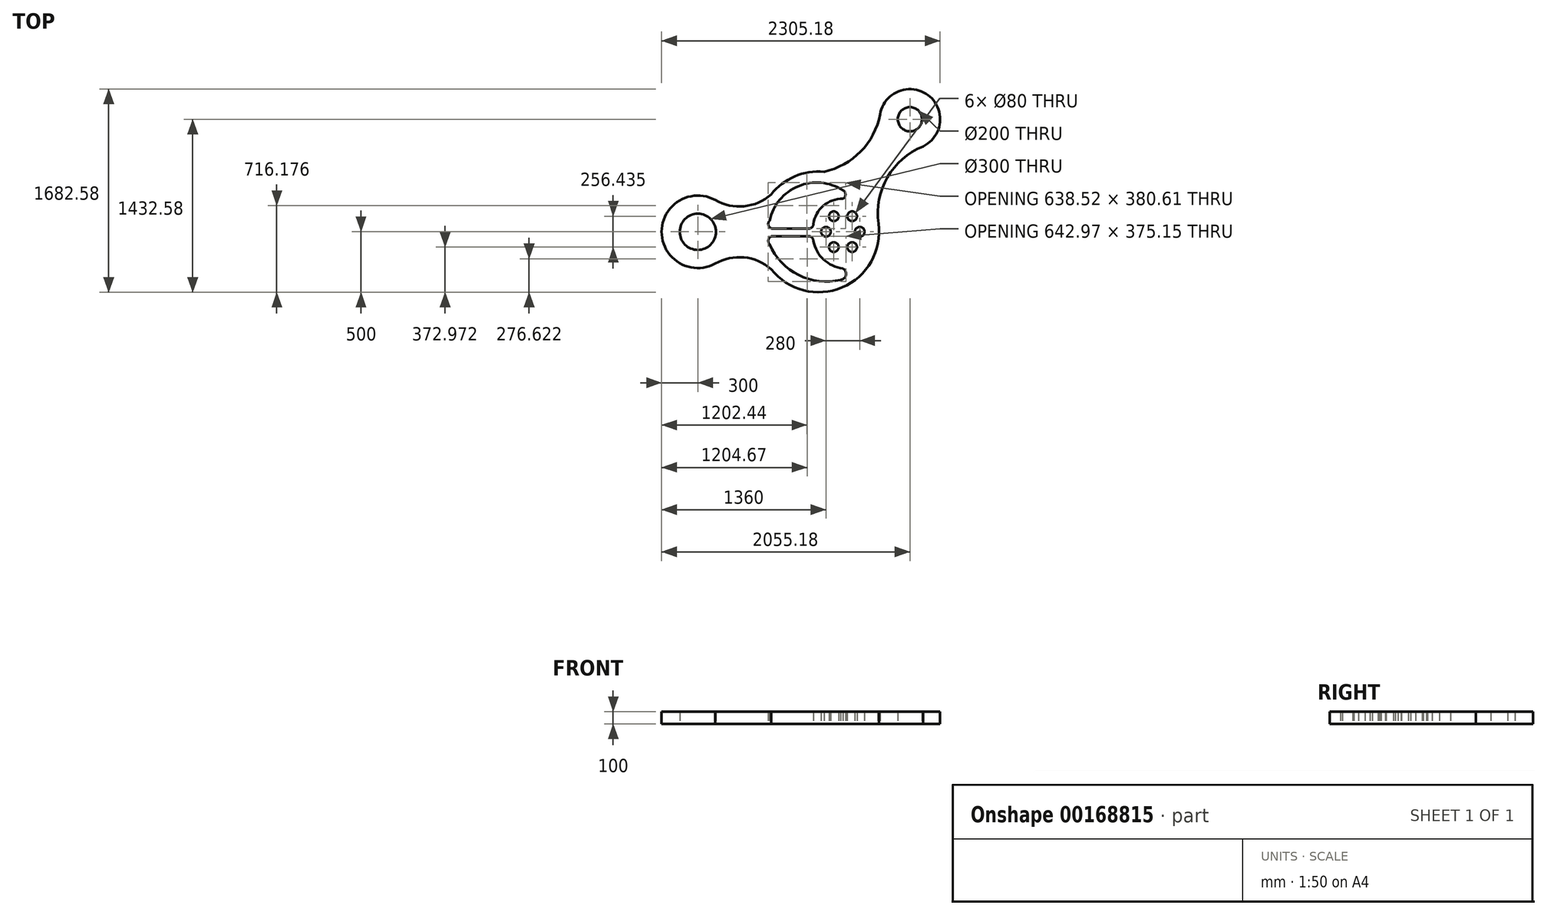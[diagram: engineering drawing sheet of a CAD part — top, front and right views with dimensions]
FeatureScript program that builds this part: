
annotation { "Feature Type Name" : "Feature", "Feature Type Description" : "" }
export const myFeature = defineFeature(function(context is Context, id is Id, definition is map)
    precondition{}
    {
        {
            var Q0;
            Q0=qCreatedBy(makeId("Top.planeOp"),FACE);
            var sketch = newSketch(context, id + "F0", { "sketchPlane" : qUnion([Q0])});
            skLineSegment(sketch, "E0", {"start": v(200, 0) * mm, "end": v(-1981.3, 0) * mm});
            skLineSegment(sketch, "E1", {"start": v(0, 0) * mm, "end": v(874.41, 1079.81) * mm});
            skCircle(sketch, "E2", {"center": v(755.18, 932.58) * mm, "radius": 100 * mm});
            skCircle(sketch, "E3", {"center": v(755.18, 932.58) * mm, "radius": 250 * mm});
            skCircle(sketch, "E4", {"center": v(0, 0) * mm, "radius": 500 * mm});
            skCircle(sketch, "E5", {"center": v(-1000, 0) * mm, "radius": 150 * mm});
            skCircle(sketch, "E6", {"center": v(-1000, 0) * mm, "radius": 300 * mm});
            skArc(sketch, "E7", {"start": v(-856.64, 263.53) * mm, "mid": v(-617.37, 211.9) * mm, "end": v(-392.82, 309.34) * mm});
            skArc(sketch, "E8", {"start": v(-392.82, -309.34) * mm, "mid": v(-617.37, -211.9) * mm, "end": v(-856.64, -263.53) * mm});
            skArc(sketch, "E9", {"start": v(43.8, 498.08) * mm, "mid": v(347.86, 665.32) * mm, "end": v(508.46, 972.94) * mm});
            skArc(sketch, "E10", {"start": v(864.48, 707.73) * mm, "mid": v(569.68, 451.16) * mm, "end": v(495.43, 67.47) * mm});
            skCircle(sketch, "E11", {"center": v(200, 0) * mm, "radius": 220 * mm});
            skCircle(sketch, "E12", {"center": v(340, 0) * mm, "radius": 40 * mm});
            skCircle(sketch, "E13", {"center": v(60, 0) * mm, "radius": 40 * mm});
            skCircle(sketch, "E14", {"center": v(125.2, -127.03) * mm, "radius": 40 * mm});
            skCircle(sketch, "E15", {"center": v(277.06, -127.03) * mm, "radius": 40 * mm});
            skCircle(sketch, "E16", {"center": v(277.06, 129.4) * mm, "radius": 40 * mm});
            skCircle(sketch, "E17", {"center": v(125.2, 129.4) * mm, "radius": 40 * mm});
            skArc(sketch, "E18", {"start": v(200, 344.87) * mm, "mid": v(-169.16, 377.43) * mm, "end": v(-406.61, 92.9) * mm});
            skLineSegment(sketch, "E19", {"start": v(-83.93, 25.87) * mm, "end": v(-377.13, 25.87) * mm});
            skArc(sketch, "E20", {"start": v(-406.61, 92.9) * mm, "mid": v(-413.75, 49.77) * mm, "end": v(-377.13, 25.87) * mm});
            skArc(sketch, "E21", {"start": v(200, 273.73) * mm, "mid": v(37.99, 215.88) * mm, "end": v(-43.95, 64.62) * mm});
            skArc(sketch, "E22", {"start": v(-83.93, 25.87) * mm, "mid": v(-56.1, 37.15) * mm, "end": v(-43.95, 64.62) * mm});
            skArc(sketch, "E23", {"start": v(200, 273.73) * mm, "mid": v(221.7, 309.3) * mm, "end": v(200, 344.87) * mm});
            skLineSegment(sketch, "E24", {"start": v(-377.13, -35.8) * mm, "end": v(-83.93, -35.8) * mm});
            skArc(sketch, "E25", {"start": v(-377.13, -35.8) * mm, "mid": v(-413.75, -59.7) * mm, "end": v(-406.61, -102.83) * mm});
            skArc(sketch, "E26", {"start": v(-43.95, -77.05) * mm, "mid": v(41.57, -229.75) * mm, "end": v(200, -304.12) * mm});
            skArc(sketch, "E27", {"start": v(-43.95, -77.05) * mm, "mid": v(-55.2, -47.96) * mm, "end": v(-83.93, -35.8) * mm});
            skArc(sketch, "E28", {"start": v(-406.61, -102.83) * mm, "mid": v(-165.7, -357.89) * mm, "end": v(182.87, -397.69) * mm});
            skArc(sketch, "E29", {"start": v(182.87, -397.69) * mm, "mid": v(225.8, -357.2) * mm, "end": v(200, -304.12) * mm});
            skSolve(sketch);
        }
        {
            var Q0;
            {var subQ1=sQuery(id+"F0.wireOp",EDGE,"E6");var subQ3=sQuery(id+"F0.wireOp",EDGE,"E0");var subQ4=makeQuery(id+"F0.imprint","INTERSECT",VERTEX,{"disambiguationData":[OD(1.0)],"derivedFrom":[subQ3,subQ1]});Q0=makeQuery(id+"F0.imprint","IMPRINT",FACE,{"disambiguationData":[TD([[makeQuery(id+"F0.imprint","IMPRINT",EDGE,{"disambiguationData":[TD([[subQ4,-1.0]])],"derivedFrom":subQ3}),-1.0]])]});}
            var Q1;
            {var subQ1=sQuery(id+"F0.wireOp",EDGE,"E6");var subQ3=sQuery(id+"F0.wireOp",EDGE,"E0");var subQ9=makeQuery(id+"F0.imprint","INTERSECT",VERTEX,{"disambiguationData":[OD(1.0)],"derivedFrom":[subQ3,subQ1]});Q1=makeQuery(id+"F0.imprint","IMPRINT",FACE,{"disambiguationData":[TD([[makeQuery(id+"F0.imprint","IMPRINT",EDGE,{"disambiguationData":[TD([[subQ9,-1.0]])],"derivedFrom":subQ3}),1.0]])]});}
            var Q2;
            {var subQ0=sQuery(id+"F0.wireOp",EDGE,"E4");var subQ1=sQuery(id+"F0.wireOp",EDGE,"E0");var subQ2=makeQuery(id+"F0.imprint","INTERSECT",VERTEX,{"derivedFrom":[subQ1,subQ0]});Q2=makeQuery(id+"F0.imprint","IMPRINT",FACE,{"disambiguationData":[TD([[makeQuery(id+"F0.imprint","IMPRINT",EDGE,{"disambiguationData":[TD([[subQ2,-1.0]])],"derivedFrom":subQ1}),1.0]])]});}
            var Q3;
            {var subQ0=sQuery(id+"F0.wireOp",EDGE,"E4");var subQ1=sQuery(id+"F0.wireOp",EDGE,"E0");var subQ2=makeQuery(id+"F0.imprint","INTERSECT",VERTEX,{"derivedFrom":[subQ1,subQ0]});Q3=makeQuery(id+"F0.imprint","IMPRINT",FACE,{"disambiguationData":[TD([[makeQuery(id+"F0.imprint","IMPRINT",EDGE,{"disambiguationData":[TD([[subQ2,-1.0]])],"derivedFrom":subQ1}),-1.0]])]});}
            var Q4;
            Q4=makeQuery(id+"F0.imprint","IMPRINT",FACE,{"disambiguationData":[TD([[makeQuery(id+"F0.imprint","IMPRINT",EDGE,{"derivedFrom":sQuery(id+"F0.wireOp",EDGE,"E18")}),-1.0]])]});
            var Q5;
            Q5=makeQuery(id+"F0.imprint","IMPRINT",FACE,{"disambiguationData":[TD([[makeQuery(id+"F0.imprint","IMPRINT",EDGE,{"derivedFrom":sQuery(id+"F0.wireOp",EDGE,"E24")}),1.0]])]});
            var Q6;
            Q6=makeQuery(id+"F0.imprint","IMPRINT",FACE,{"disambiguationData":[TD([[makeQuery(id+"F0.imprint","IMPRINT",EDGE,{"derivedFrom":sQuery(id+"F0.wireOp",EDGE,"E12")}),-1.0]])]});
            var Q7;
            {var subQ1=sQuery(id+"F0.wireOp",EDGE,"E0");var subQ3=sQuery(id+"F0.wireOp",EDGE,"E1");var subQ7=makeQuery(id+"F0.imprint","INTERSECT",VERTEX,{"derivedFrom":[subQ1,subQ3]});Q7=makeQuery(id+"F0.imprint","IMPRINT",FACE,{"disambiguationData":[TD([[makeQuery(id+"F0.imprint","IMPRINT",EDGE,{"disambiguationData":[TD([[subQ7,-1.0]])],"derivedFrom":subQ1}),-1.0]])]});}
            var Q8;
            {var subQ0=sQuery(id+"F0.wireOp",EDGE,"E3");var subQ1=sQuery(id+"F0.wireOp",EDGE,"E1");var subQ2=makeQuery(id+"F0.imprint","INTERSECT",VERTEX,{"derivedFrom":[subQ1,subQ0]});Q8=makeQuery(id+"F0.imprint","IMPRINT",FACE,{"disambiguationData":[TD([[makeQuery(id+"F0.imprint","IMPRINT",EDGE,{"disambiguationData":[TD([[subQ2,1.0]])],"derivedFrom":subQ1}),-1.0]])]});}
            var Q9;
            {var subQ5=sQuery(id+"F0.wireOp",EDGE,"E9");Q9=makeQuery(id+"F0.imprint","IMPRINT",FACE,{"disambiguationData":[TD([[makeQuery(id+"F0.imprint","IMPRINT",EDGE,{"derivedFrom":subQ5}),-1.0]])]});}
            var Q10;
            {var subQ1=sQuery(id+"F0.wireOp",EDGE,"E1");var subQ6=sQuery(id+"F0.wireOp",EDGE,"E2");var subQ7=makeQuery(id+"F0.imprint","INTERSECT",VERTEX,{"disambiguationData":[OD(0.0)],"derivedFrom":[subQ1,subQ6]});Q10=makeQuery(id+"F0.imprint","IMPRINT",FACE,{"disambiguationData":[TD([[makeQuery(id+"F0.imprint","IMPRINT",EDGE,{"disambiguationData":[TD([[subQ7,1.0]])],"derivedFrom":subQ6}),-1.0]])]});}
            extrude(context, id + "F1", {"entities" : qUnion([Q0, Q1, Q2, Q3, Q4, Q5, Q6, Q7, Q8, Q9, Q10]), "depth" : 100 * mm});
        }
    });
